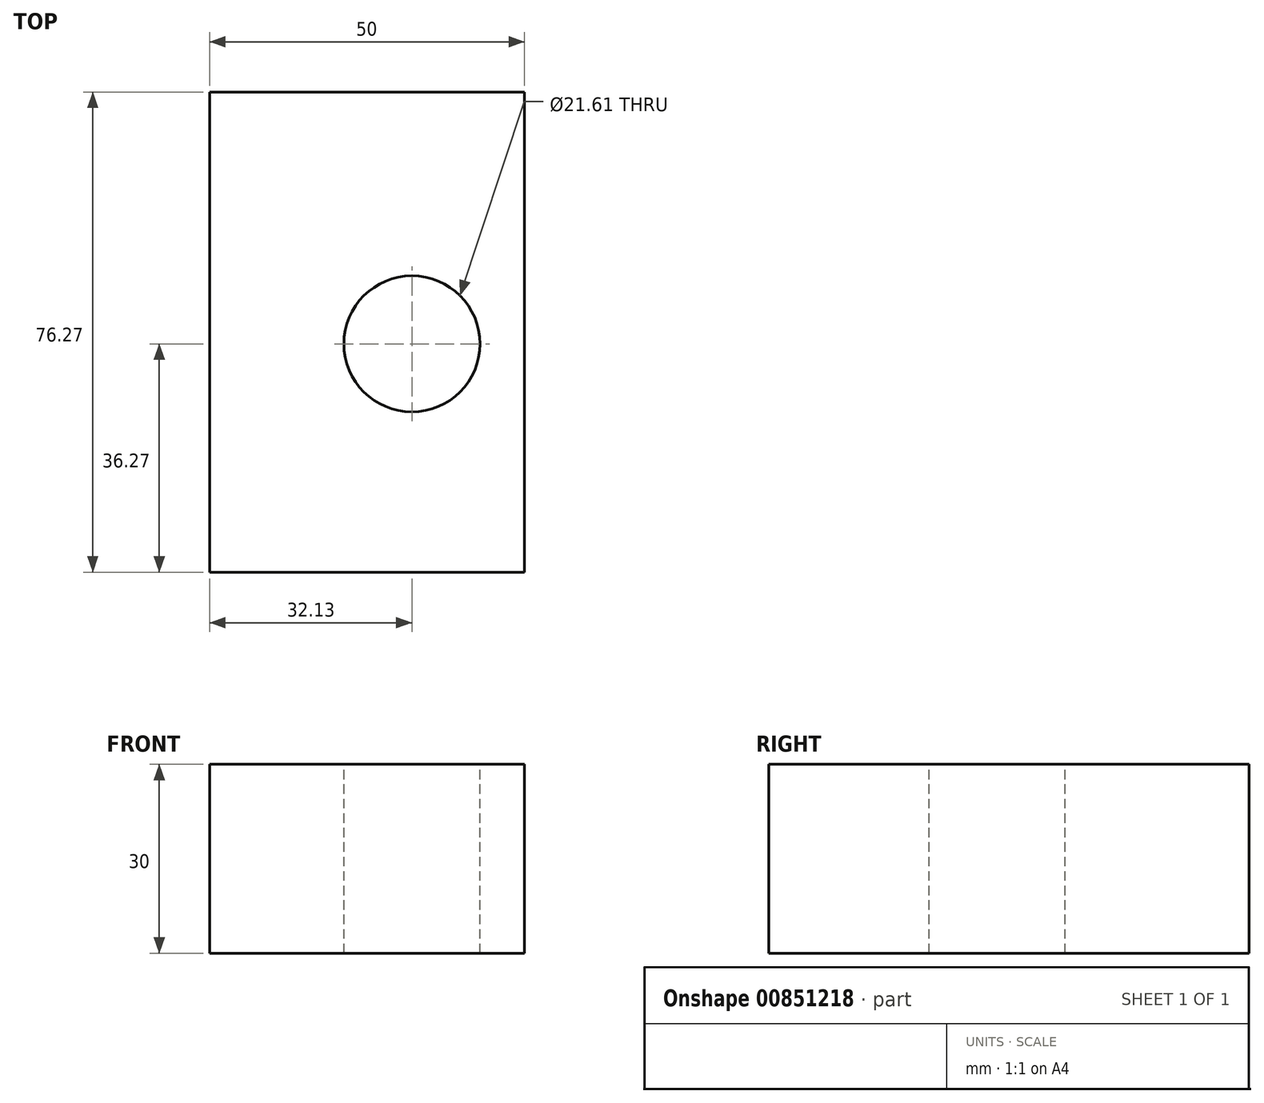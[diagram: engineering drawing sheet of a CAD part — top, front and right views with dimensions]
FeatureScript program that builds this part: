
annotation { "Feature Type Name" : "Feature", "Feature Type Description" : "" }
export const myFeature = defineFeature(function(context is Context, id is Id, definition is map)
    precondition{}
    {
        {
            var Q0;
            Q0=qCreatedBy(makeId("Front.planeOp"),FACE);
            var sketch = newSketch(context, id + "F0", { "sketchPlane" : qUnion([Q0])});
            skLineSegment(sketch, "E0.bottom", {"start": v(-62.13, 41.14) * mm, "end": v(-12.13, 41.14) * mm});
            skLineSegment(sketch, "E0.top", {"start": v(-62.13, 11.14) * mm, "end": v(-12.13, 11.14) * mm});
            skLineSegment(sketch, "E0.left", {"start": v(-62.13, 41.14) * mm, "end": v(-62.13, 11.14) * mm});
            skLineSegment(sketch, "E0.right", {"start": v(-12.13, 41.14) * mm, "end": v(-12.13, 11.14) * mm});
            skSolve(sketch);
        }
        {
            var Q0;
            Q0=makeQuery(id+"F0.imprint","IMPRINT",FACE,{"disambiguationData":[TD([[makeQuery(id+"F0.imprint","IMPRINT",EDGE,{"derivedFrom":sQuery(id+"F0.wireOp",EDGE,"E0.bottom")}),-1.0]])]});
            var Q1;
            Q1 = qSketchRegion(id + "F0", true);
            extrude(context, id + "F1", {"entities" : qUnion([Q0, Q1]), "depth" : 76.27 * mm, "offsetDistance" : 25 * mm});
        }
        {
            var Q0;
            Q0=makeQuery(id+"F1.opExtrude","SWEPT_FACE",FACE,{"disambiguationData":[OSD([sQuery(id+"F0.wireOp",EDGE,"E0.bottom")])]});
            var sketch = newSketch(context, id + "F2", { "sketchPlane" : qUnion([Q0])});
            skCircle(sketch, "E1", {"center": v(-30, -40) * mm, "radius": 10.8 * mm});
            skSolve(sketch);
        }
        {
            var Q0;
            Q0=makeQuery(id+"F2.imprint","IMPRINT",FACE,{"disambiguationData":[TD([[makeQuery(id+"F2.imprint","IMPRINT",EDGE,{"derivedFrom":sQuery(id+"F2.wireOp",EDGE,"E1")}),1.0]])]});
            var Q1;
            Q1 = qSketchRegion(id + "F2", true);
            extrude(context, id + "F3", {"entities" : qUnion([Q0, Q1]), "operationType" : NewBodyOperationType.REMOVE, "endBound" : BoundingType.THROUGH_ALL, "oppositeDirection" : true, "depth" : 25 * mm, "offsetDistance" : 25 * mm});
        }
    });
